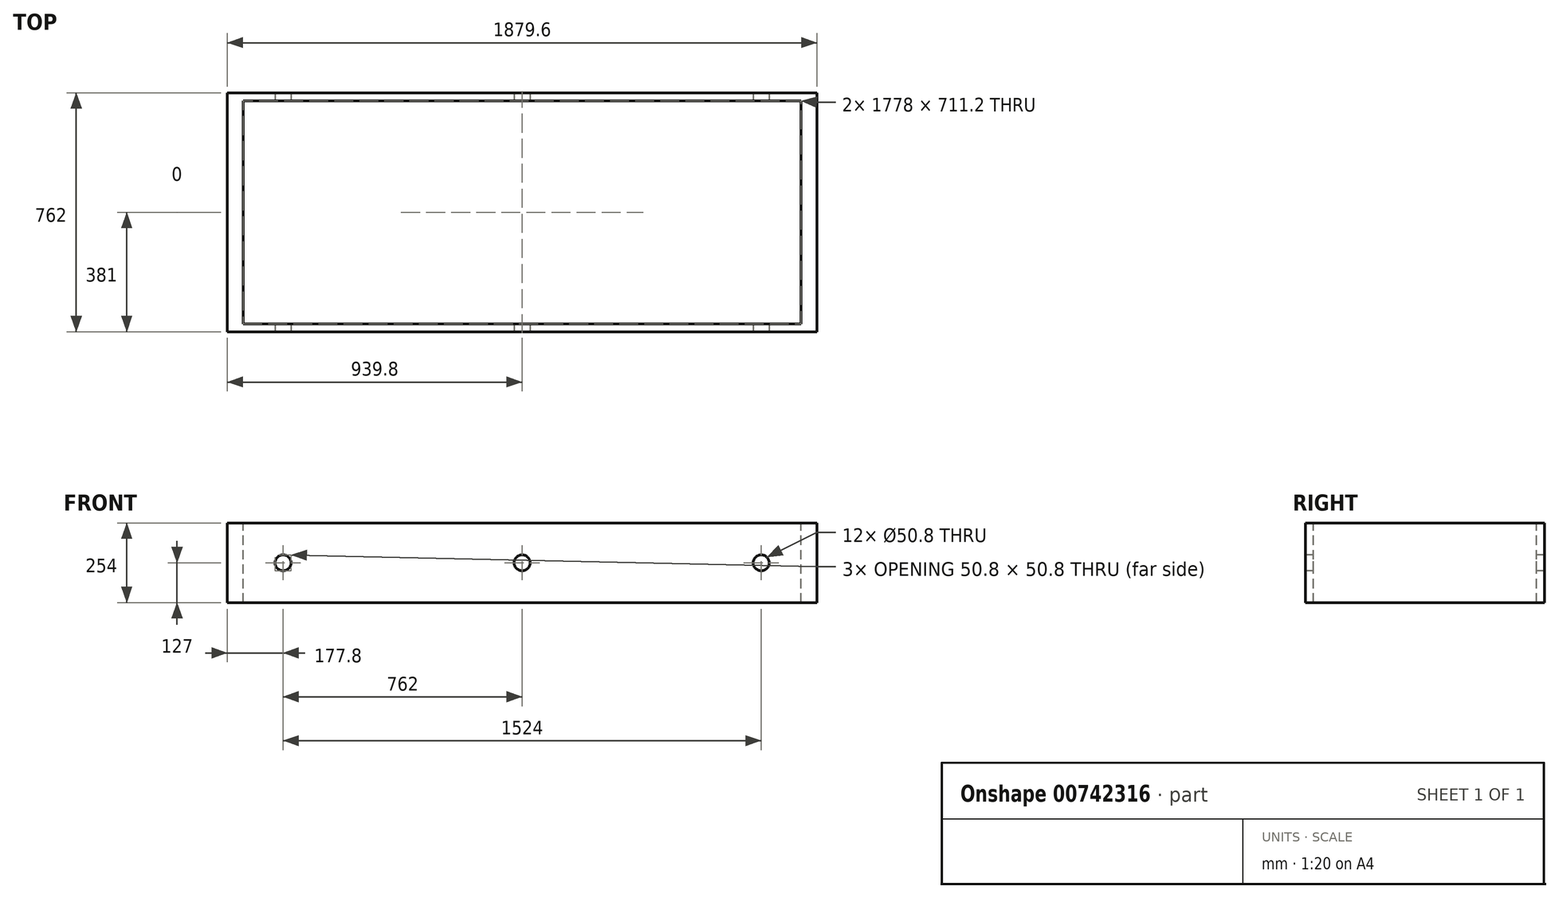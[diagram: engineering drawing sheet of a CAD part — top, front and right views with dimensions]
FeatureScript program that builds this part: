
annotation { "Feature Type Name" : "Feature", "Feature Type Description" : "" }
export const myFeature = defineFeature(function(context is Context, id is Id, definition is map)
    precondition{}
    {
        {
            var Q0;
            Q0=qCreatedBy(makeId("Top.planeOp"),FACE);
            var sketch = newSketch(context, id + "F0", { "sketchPlane" : qUnion([Q0])});
            skLineSegment(sketch, "E0.bottom", {"start": v(-939.8, 381) * mm, "end": v(939.8, 381) * mm});
            skLineSegment(sketch, "E0.top", {"start": v(-939.8, -381) * mm, "end": v(939.8, -381) * mm});
            skLineSegment(sketch, "E0.left", {"start": v(-939.8, 381) * mm, "end": v(-939.8, -381) * mm});
            skLineSegment(sketch, "E0.right", {"start": v(939.8, 381) * mm, "end": v(939.8, -381) * mm});
            skSolve(sketch);
        }
        {
            var Q0;
            Q0=qSketchRegion(id+"F0",true);
            extrude(context, id + "F1", {"entities" : qUnion([Q0]), "endBound" : BoundingType.SYMMETRIC, "depth" : 254 * mm, "offsetDistance" : 25.4 * mm});
        }
        {
            var Q0;
            Q0=makeQuery(id+"F1.opExtrude","CAP_FACE",FACE,{"disambiguationData":[OSD([sQuery(id+"F0.wireOp",EDGE,"E0.bottom"),sQuery(id+"F0.wireOp",EDGE,"E0.top"),sQuery(id+"F0.wireOp",EDGE,"E0.left"),sQuery(id+"F0.wireOp",EDGE,"E0.right")])],"isStart":false});
            var sketch = newSketch(context, id + "F2", { "sketchPlane" : qUnion([Q0])});
            skLineSegment(sketch, "E1.bottom", {"start": v(-889, 355.6) * mm, "end": v(889, 355.6) * mm});
            skLineSegment(sketch, "E1.top", {"start": v(-889, -355.6) * mm, "end": v(889, -355.6) * mm});
            skLineSegment(sketch, "E1.left", {"start": v(-889, 355.6) * mm, "end": v(-889, -355.6) * mm});
            skLineSegment(sketch, "E1.right", {"start": v(889, 355.6) * mm, "end": v(889, -355.6) * mm});
            skSolve(sketch);
        }
        {
            var Q0;
            Q0=qSketchRegion(id+"F2",true);
            var Q1;
            Q1=qSketchRegion(id+"F4",true);
            extrude(context, id + "F3", {"entities" : qUnion([Q0, Q1]), "operationType" : NewBodyOperationType.REMOVE, "endBound" : BoundingType.SYMMETRIC, "oppositeDirection" : true, "depth" : 1270 * mm, "offsetDistance" : 25.4 * mm});
        }
        {
            var Q0;
            Q0=makeQuery(id+"F1.opExtrude","SWEPT_FACE",FACE,{"disambiguationData":[OSD([sQuery(id+"F0.wireOp",EDGE,"E0.top")])]});
            var sketch = newSketch(context, id + "F4", { "sketchPlane" : qUnion([Q0])});
            skCircle(sketch, "E2", {"center": v(-762, 0) * mm, "radius": 25.4 * mm});
            skCircle(sketch, "E3", {"center": v(762, 0) * mm, "radius": 25.4 * mm});
            skCircle(sketch, "E4", {"center": v(0, 0) * mm, "radius": 25.4 * mm});
            skSolve(sketch);
        }
        {
            var Q0;
            Q0=qSketchRegion(id+"F4",true);
            extrude(context, id + "F5", {"entities" : qUnion([Q0]), "operationType" : NewBodyOperationType.REMOVE, "endBound" : BoundingType.THROUGH_ALL, "oppositeDirection" : true, "depth" : 25.4 * mm, "offsetDistance" : 25.4 * mm});
        }
    });
